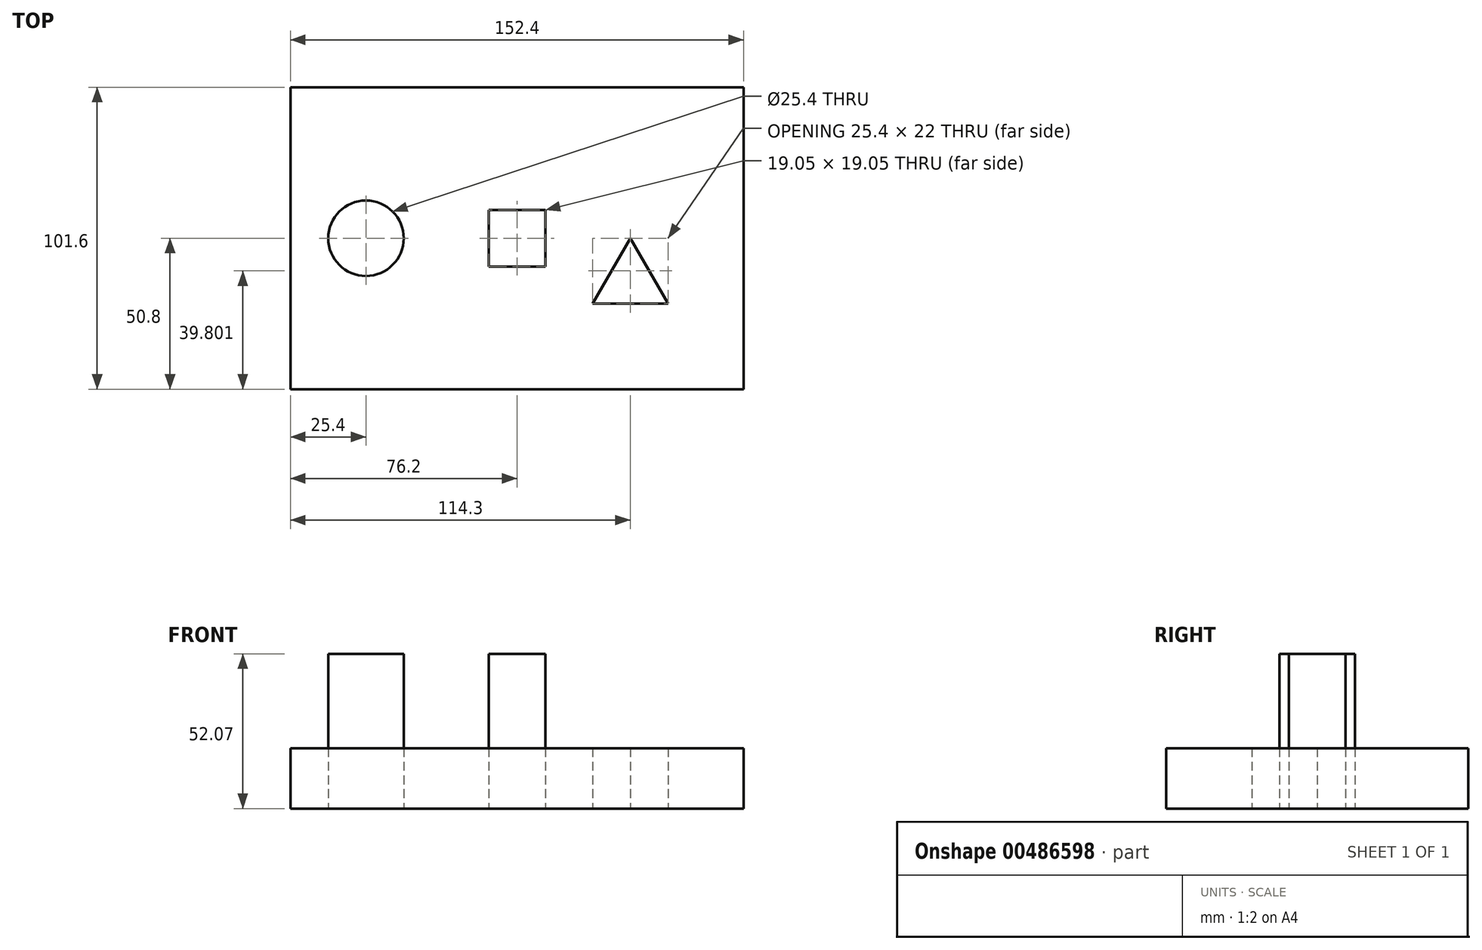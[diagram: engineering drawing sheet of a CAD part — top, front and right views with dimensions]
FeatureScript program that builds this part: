
annotation { "Feature Type Name" : "Feature", "Feature Type Description" : "" }
export const myFeature = defineFeature(function(context is Context, id is Id, definition is map)
    precondition{}
    {
        {
            var Q0;
            Q0=qCreatedBy(makeId("Top.planeOp"),FACE);
            var sketch = newSketch(context, id + "F0", { "sketchPlane" : qUnion([Q0])});
            skLineSegment(sketch, "E0", {"start": v(0, 0) * mm, "end": v(6.35, 0) * mm});
            skCircle(sketch, "E1.cCircle", {"center": v(6.35, -14.66) * mm, "radius": 14.66 * mm, "construction": true});
            skLineSegment(sketch, "E1.0", {"start": v(6.35, 0) * mm, "end": v(19.05, -22) * mm});
            skLineSegment(sketch, "E1.1", {"start": v(19.05, -22) * mm, "end": v(-6.35, -22) * mm});
            skLineSegment(sketch, "E1.2", {"start": v(-6.35, -22) * mm, "end": v(6.35, 0) * mm});
            skLineSegment(sketch, "E2", {"start": v(0, 0) * mm, "end": v(-31.75, 0) * mm});
            skLineSegment(sketch, "E3.bottom", {"start": v(-41.27, 9.53) * mm, "end": v(-22.22, 9.53) * mm});
            skLineSegment(sketch, "E3.top", {"start": v(-41.28, -9.52) * mm, "end": v(-22.23, -9.52) * mm});
            skLineSegment(sketch, "E3.left", {"start": v(-41.27, 9.53) * mm, "end": v(-41.27, -9.52) * mm});
            skLineSegment(sketch, "E3.right", {"start": v(-22.22, 9.53) * mm, "end": v(-22.23, -9.52) * mm});
            skPoint(sketch, "E3.middle", {"position": v(-31.75, 0) * mm});
            skLineSegment(sketch, "E4", {"start": v(-31.75, 0) * mm, "end": v(-82.55, 0) * mm});
            skCircle(sketch, "E5", {"center": v(-82.55, 0) * mm, "radius": 12.7 * mm});
            skLineSegment(sketch, "E6", {"start": v(0, 0) * mm, "end": v(44.45, 0) * mm});
            skLineSegment(sketch, "E7.bottom", {"start": v(44.45, 50.8) * mm, "end": v(-107.95, 50.8) * mm});
            skLineSegment(sketch, "E7.top", {"start": v(44.45, -50.8) * mm, "end": v(-107.95, -50.8) * mm});
            skLineSegment(sketch, "E7.left", {"start": v(44.45, 50.8) * mm, "end": v(44.45, -50.8) * mm});
            skLineSegment(sketch, "E7.right", {"start": v(-107.95, 50.8) * mm, "end": v(-107.95, -50.8) * mm});
            skSolve(sketch);
        }
        {
            var Q0;
            Q0 = qSketchRegion(id + "F0", true);
            extrude(context, id + "F1", {"entities" : qUnion([Q0]), "depth" : 20.32 * mm});
        }
        {
            var Q0;
            {var subQ1=sQuery(id+"F0.wireOp",EDGE,"E3.bottom");Q0=makeQuery(id+"F0.imprint","IMPRINT",FACE,{"disambiguationData":[TD([[makeQuery(id+"F0.imprint","IMPRINT",EDGE,{"derivedFrom":subQ1}),-1.0]])]});}
            var Q1;
            {var subQ1=sQuery(id+"F0.wireOp",EDGE,"E3.top");Q1=makeQuery(id+"F0.imprint","IMPRINT",FACE,{"disambiguationData":[TD([[makeQuery(id+"F0.imprint","IMPRINT",EDGE,{"derivedFrom":subQ1}),1.0]])]});}
            var Q2;
            Q2=makeQuery(id+"F0.imprint","IMPRINT",FACE,{"disambiguationData":[TD([[makeQuery(id+"F0.imprint","IMPRINT",EDGE,{"derivedFrom":sQuery(id+"F0.wireOp",EDGE,"E5")}),1.0]])]});
            extrude(context, id + "F2", {"entities" : qUnion([Q0, Q1, Q2]), "depth" : 52.07 * mm});
        }
    });
